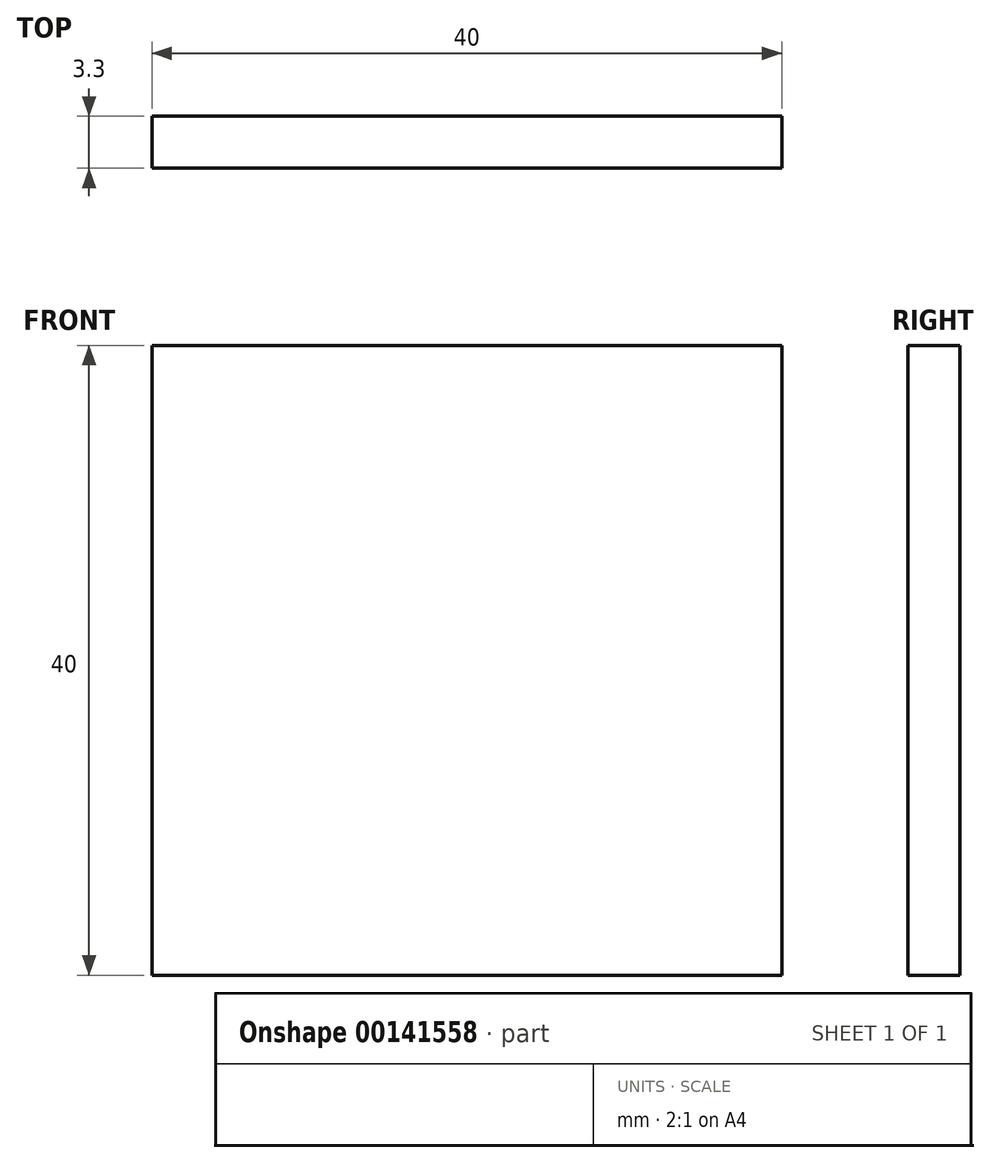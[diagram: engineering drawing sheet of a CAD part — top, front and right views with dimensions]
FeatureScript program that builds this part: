
annotation { "Feature Type Name" : "Feature", "Feature Type Description" : "" }
export const myFeature = defineFeature(function(context is Context, id is Id, definition is map)
    precondition{}
    {
        {
            var Q0;
            Q0=qCreatedBy(makeId("Front.planeOp"),FACE);
            var sketch = newSketch(context, id + "F0", { "sketchPlane" : qUnion([Q0])});
            skLineSegment(sketch, "E0.bottom", {"start": v(20, -20) * mm, "end": v(-20, -20) * mm});
            skLineSegment(sketch, "E0.top", {"start": v(20, 20) * mm, "end": v(-20, 20) * mm});
            skLineSegment(sketch, "E0.left", {"start": v(20, -20) * mm, "end": v(20, 20) * mm});
            skLineSegment(sketch, "E0.right", {"start": v(-20, -20) * mm, "end": v(-20, 20) * mm});
            skPoint(sketch, "E0.middle", {"position": v(0, 0) * mm});
            skSolve(sketch);
        }
        {
            var Q0;
            Q0 = qSketchRegion(id + "F0", true);
            extrude(context, id + "F1", {"entities" : qUnion([Q0]), "depth" : 3.3 * mm});
        }
    });
